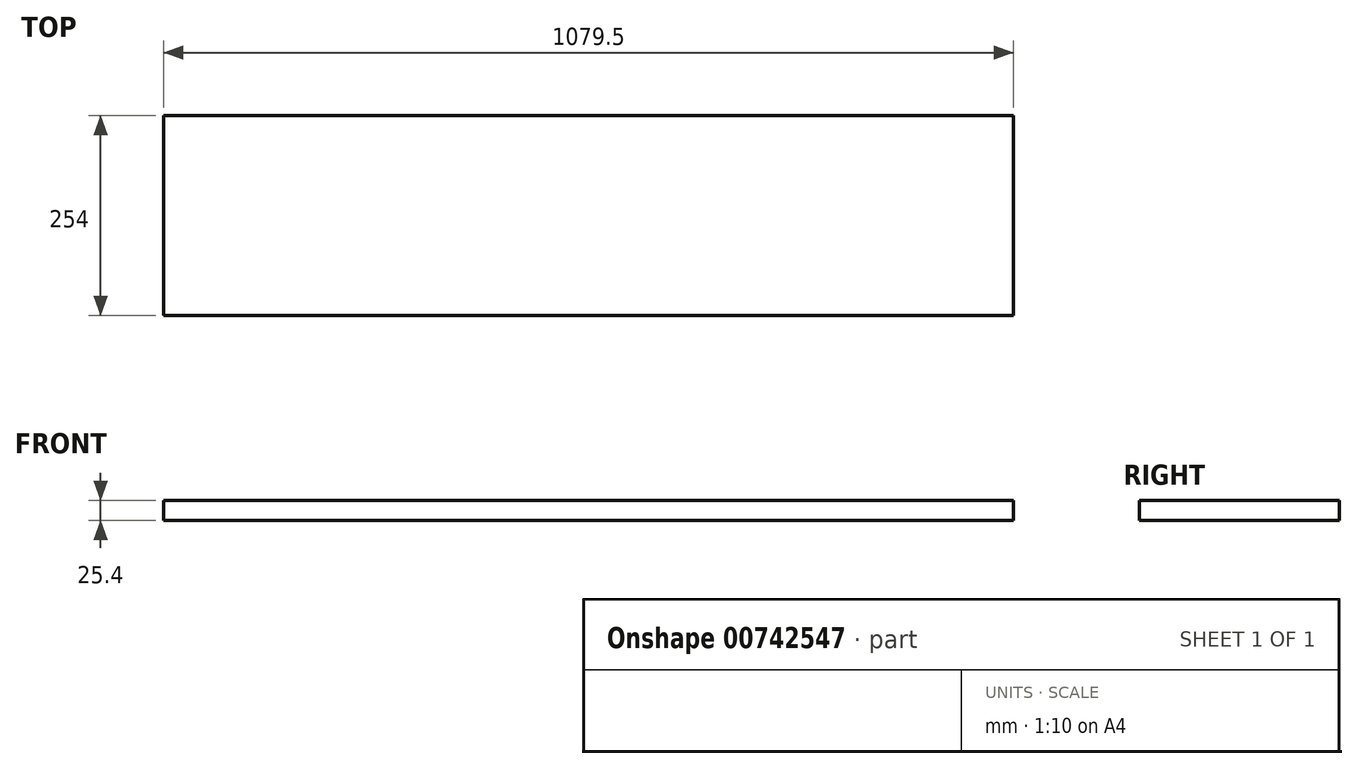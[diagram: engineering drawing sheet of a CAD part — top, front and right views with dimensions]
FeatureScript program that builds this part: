
annotation { "Feature Type Name" : "Feature", "Feature Type Description" : "" }
export const myFeature = defineFeature(function(context is Context, id is Id, definition is map)
    precondition{}
    {
        {
            var Q0;
            Q0=qCreatedBy(makeId("Top.planeOp"),FACE);
            var sketch = newSketch(context, id + "F0", { "sketchPlane" : qUnion([Q0])});
            skLineSegment(sketch, "E0.bottom", {"start": v(539.75, 127) * mm, "end": v(-539.75, 127) * mm});
            skLineSegment(sketch, "E0.top", {"start": v(539.75, -127) * mm, "end": v(-539.75, -127) * mm});
            skLineSegment(sketch, "E0.left", {"start": v(539.75, 127) * mm, "end": v(539.75, -127) * mm});
            skLineSegment(sketch, "E0.right", {"start": v(-539.75, 127) * mm, "end": v(-539.75, -127) * mm});
            skPoint(sketch, "E0.middle", {"position": v(0, 0) * mm});
            skSolve(sketch);
        }
        {
            var Q0;
            Q0 = qSketchRegion(id + "F0", true);
            extrude(context, id + "F1", {"entities" : qUnion([Q0]), "depth" : 25.4 * mm, "offsetDistance" : 25.4 * mm});
        }
    });
